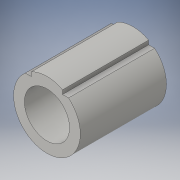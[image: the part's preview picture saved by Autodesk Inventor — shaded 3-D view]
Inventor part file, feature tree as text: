
AUTODESK INVENTOR PART (.ipt)
format: ipt  version: 2016 (Build 200138000, 138)  size: 112,640 bytes
history: native  units: in
note: dims shown in document units (in); Inventor stores cm internally (conversion verified against a paired STEP export)
features: extrude x2, sketch x2
ambient origin geometry x8: Origin, YZ Plane, XZ Plane, XY Plane, X Axis, Y Axis, Z Axis, Center Point
bodies: Solid1 (feature_tree)
feature tree (4):
  extrude  "Extrusion1"  Depth=1.55in
  extrude  "Extrusion2"  Depth=2.0in
  sketch  "Sketch1"  dims[d0=1.05in d1=1.55in]
  sketch  "Sketch2"  dims[d2=2.0in d3=0.0in d4=0.15in d5=0.362in d6=0.15in d7=0.362in d8=2.0in d9=0.0in]
